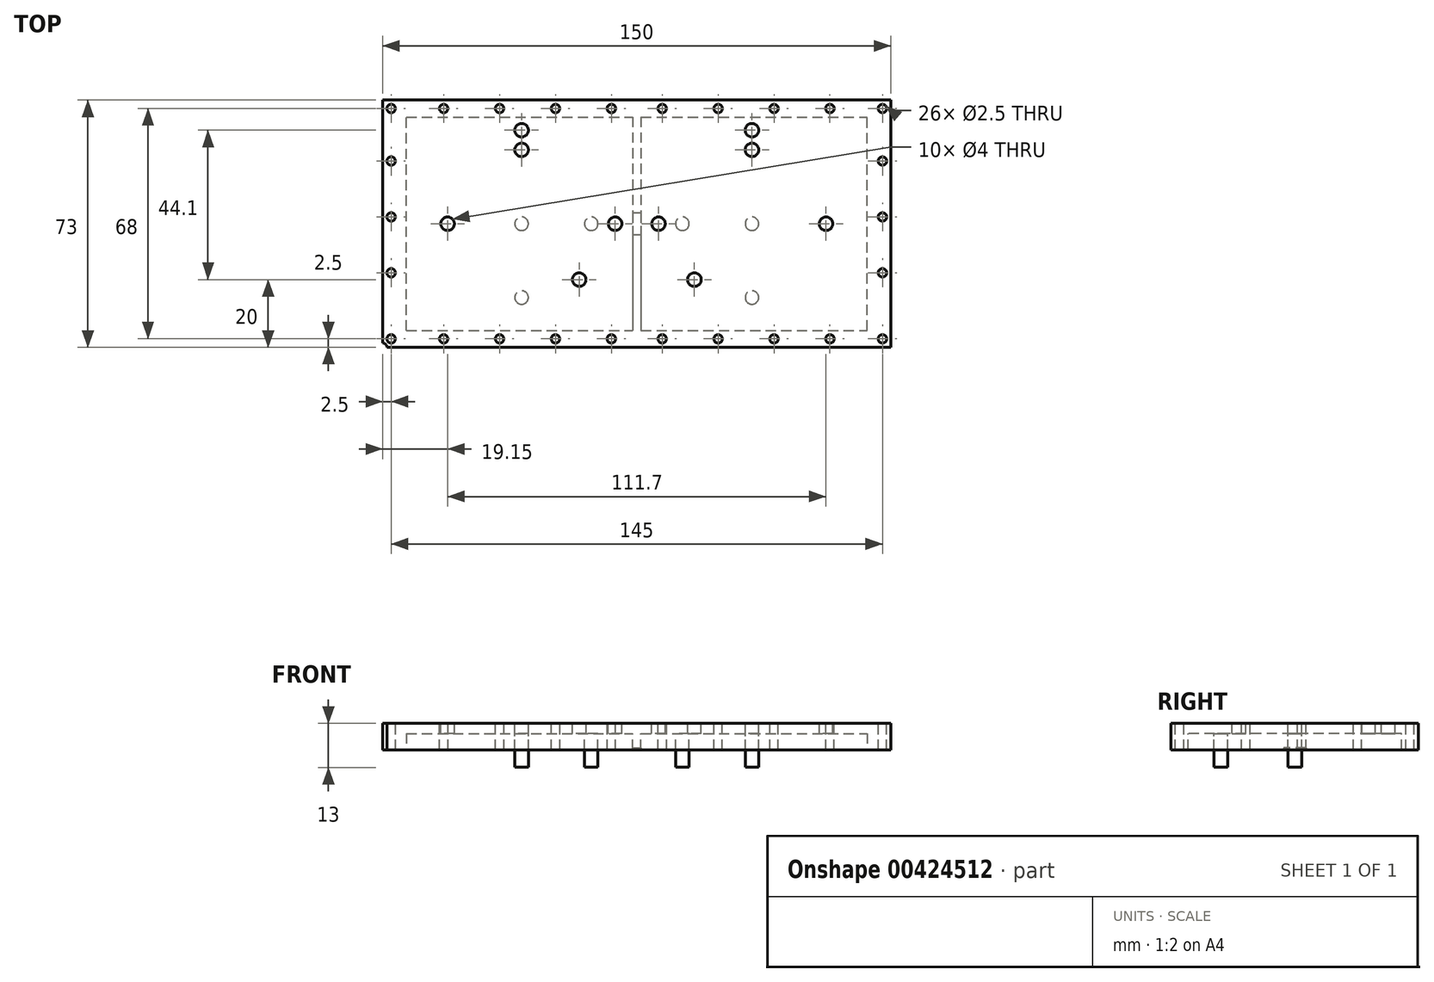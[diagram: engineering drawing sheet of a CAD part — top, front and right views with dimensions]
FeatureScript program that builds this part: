
annotation { "Feature Type Name" : "Feature", "Feature Type Description" : "" }
export const myFeature = defineFeature(function(context is Context, id is Id, definition is map)
    precondition{}
    {
        {
            var Q0;
            Q0=qCreatedBy(makeId("Top.planeOp"),FACE);
            var sketch = newSketch(context, id + "F0", { "sketchPlane" : qUnion([Q0])});
            skLineSegment(sketch, "E0.bottom", {"start": v(0, 0) * mm, "end": v(150, 0) * mm});
            skLineSegment(sketch, "E0.top", {"start": v(0, 73) * mm, "end": v(150, 73) * mm});
            skLineSegment(sketch, "E0.left", {"start": v(0, 0) * mm, "end": v(0, 73) * mm});
            skLineSegment(sketch, "E0.right", {"start": v(150, 0) * mm, "end": v(150, 73) * mm});
            skSolve(sketch);
        }
        {
            var Q0;
            Q0=qSketchRegion(id+"F0",true);
            extrude(context, id + "F1", {"entities" : qUnion([Q0]), "depth" : 7.87 * mm});
        }
        {
            var Q0;
            Q0=qCreatedBy(makeId("Top.planeOp"),FACE);
            var sketch = newSketch(context, id + "F2", { "sketchPlane" : qUnion([Q0])});
            skLineSegment(sketch, "E1.bottom", {"start": v(7, 5) * mm, "end": v(143, 5) * mm});
            skLineSegment(sketch, "E1.top", {"start": v(7, 68) * mm, "end": v(143, 68) * mm});
            skLineSegment(sketch, "E1.left", {"start": v(7, 5) * mm, "end": v(7, 68) * mm});
            skLineSegment(sketch, "E1.right", {"start": v(143, 5) * mm, "end": v(143, 68) * mm});
            skSolve(sketch);
        }
        {
            var Q0;
            Q0=qSketchRegion(id+"F2",true);
            extrude(context, id + "F3", {"entities" : qUnion([Q0]), "operationType" : NewBodyOperationType.REMOVE, "depth" : 4.87 * mm});
        }
        {
            var Q0;
            Q0=makeQuery(id+"F1.opExtrude","CAP_FACE",FACE,{"disambiguationData":[OSD([sQuery(id+"F0.wireOp",EDGE,"E0.bottom"),sQuery(id+"F0.wireOp",EDGE,"E0.top"),sQuery(id+"F0.wireOp",EDGE,"E0.left"),sQuery(id+"F0.wireOp",EDGE,"E0.right")])],"isStart":false});
            var sketch = newSketch(context, id + "F4", { "sketchPlane" : qUnion([Q0])});
            skCircle(sketch, "E2", {"center": v(2.5, 2.5) * mm, "radius": 1.25 * mm});
            skSolve(sketch);
        }
        {
            var Q0;
            Q0=qSketchRegion(id+"F4",true);
            extrude(context, id + "F5", {"entities" : qUnion([Q0]), "operationType" : NewBodyOperationType.REMOVE, "oppositeDirection" : true, "depth" : 7.87 * mm});
        }
        {
            var Q0;
            Q0=makeQuery(id+"F1.opExtrude","CAP_FACE",FACE,{"disambiguationData":[OSD([sQuery(id+"F0.wireOp",EDGE,"E0.bottom"),sQuery(id+"F0.wireOp",EDGE,"E0.top"),sQuery(id+"F0.wireOp",EDGE,"E0.left"),sQuery(id+"F0.wireOp",EDGE,"E0.right")])],"isStart":false});
            var sketch = newSketch(context, id + "F6", { "sketchPlane" : qUnion([Q0])});
            skCircle(sketch, "E3", {"center": v(18, 2.5) * mm, "radius": 1.25 * mm});
            skSolve(sketch);
        }
        {
            var Q0;
            Q0=qSketchRegion(id+"F6",true);
            extrude(context, id + "F7", {"entities" : qUnion([Q0]), "operationType" : NewBodyOperationType.REMOVE, "oppositeDirection" : true, "depth" : 7.87 * mm});
        }
        {
            var Q0;
            Q0=makeQuery(id+"F1.opExtrude","CAP_FACE",FACE,{"disambiguationData":[OSD([sQuery(id+"F0.wireOp",EDGE,"E0.bottom"),sQuery(id+"F0.wireOp",EDGE,"E0.top"),sQuery(id+"F0.wireOp",EDGE,"E0.left"),sQuery(id+"F0.wireOp",EDGE,"E0.right")])],"isStart":false});
            var sketch = newSketch(context, id + "F8", { "sketchPlane" : qUnion([Q0])});
            skCircle(sketch, "E4", {"center": v(34.5, 2.5) * mm, "radius": 1.25 * mm});
            skSolve(sketch);
        }
        {
            var Q0;
            Q0=qSketchRegion(id+"F8",true);
            extrude(context, id + "F9", {"entities" : qUnion([Q0]), "operationType" : NewBodyOperationType.REMOVE, "oppositeDirection" : true, "depth" : 7.87 * mm});
        }
        {
            var Q0;
            Q0=makeQuery(id+"F1.opExtrude","CAP_FACE",FACE,{"disambiguationData":[OSD([sQuery(id+"F0.wireOp",EDGE,"E0.bottom"),sQuery(id+"F0.wireOp",EDGE,"E0.top"),sQuery(id+"F0.wireOp",EDGE,"E0.left"),sQuery(id+"F0.wireOp",EDGE,"E0.right")])],"isStart":false});
            var sketch = newSketch(context, id + "F10", { "sketchPlane" : qUnion([Q0])});
            skCircle(sketch, "E5", {"center": v(51, 2.5) * mm, "radius": 1.25 * mm});
            skSolve(sketch);
        }
        {
            var Q0;
            Q0=qSketchRegion(id+"F10",true);
            extrude(context, id + "F11", {"entities" : qUnion([Q0]), "operationType" : NewBodyOperationType.REMOVE, "oppositeDirection" : true, "depth" : 7.87 * mm});
        }
        {
            var Q0;
            Q0=makeQuery(id+"F1.opExtrude","CAP_FACE",FACE,{"disambiguationData":[OSD([sQuery(id+"F0.wireOp",EDGE,"E0.bottom"),sQuery(id+"F0.wireOp",EDGE,"E0.top"),sQuery(id+"F0.wireOp",EDGE,"E0.left"),sQuery(id+"F0.wireOp",EDGE,"E0.right")])],"isStart":false});
            var sketch = newSketch(context, id + "F12", { "sketchPlane" : qUnion([Q0])});
            skCircle(sketch, "E6", {"center": v(67.5, 2.5) * mm, "radius": 1.25 * mm});
            skSolve(sketch);
        }
        {
            var Q0;
            Q0=qSketchRegion(id+"F12",true);
            extrude(context, id + "F13", {"entities" : qUnion([Q0]), "operationType" : NewBodyOperationType.REMOVE, "oppositeDirection" : true, "depth" : 7.87 * mm});
        }
        {
            var Q0;
            Q0=makeQuery(id+"F1.opExtrude","CAP_FACE",FACE,{"disambiguationData":[OSD([sQuery(id+"F0.wireOp",EDGE,"E0.bottom"),sQuery(id+"F0.wireOp",EDGE,"E0.top"),sQuery(id+"F0.wireOp",EDGE,"E0.left"),sQuery(id+"F0.wireOp",EDGE,"E0.right")])],"isStart":false});
            var sketch = newSketch(context, id + "F14", { "sketchPlane" : qUnion([Q0])});
            skCircle(sketch, "E7", {"center": v(82.5, 2.5) * mm, "radius": 1.25 * mm});
            skSolve(sketch);
        }
        {
            var Q0;
            Q0=qSketchRegion(id+"F14",true);
            extrude(context, id + "F15", {"entities" : qUnion([Q0]), "operationType" : NewBodyOperationType.REMOVE, "oppositeDirection" : true, "depth" : 7.87 * mm});
        }
        {
            var Q0;
            Q0=makeQuery(id+"F1.opExtrude","CAP_FACE",FACE,{"disambiguationData":[OSD([sQuery(id+"F0.wireOp",EDGE,"E0.bottom"),sQuery(id+"F0.wireOp",EDGE,"E0.top"),sQuery(id+"F0.wireOp",EDGE,"E0.left"),sQuery(id+"F0.wireOp",EDGE,"E0.right")])],"isStart":false});
            var sketch = newSketch(context, id + "F16", { "sketchPlane" : qUnion([Q0])});
            skCircle(sketch, "E8", {"center": v(99, 2.5) * mm, "radius": 1.25 * mm});
            skSolve(sketch);
        }
        {
            var Q0;
            Q0=qSketchRegion(id+"F16",true);
            extrude(context, id + "F17", {"entities" : qUnion([Q0]), "operationType" : NewBodyOperationType.REMOVE, "oppositeDirection" : true, "depth" : 7.87 * mm});
        }
        {
            var Q0;
            Q0=makeQuery(id+"F1.opExtrude","CAP_FACE",FACE,{"disambiguationData":[OSD([sQuery(id+"F0.wireOp",EDGE,"E0.bottom"),sQuery(id+"F0.wireOp",EDGE,"E0.top"),sQuery(id+"F0.wireOp",EDGE,"E0.left"),sQuery(id+"F0.wireOp",EDGE,"E0.right")])],"isStart":false});
            var sketch = newSketch(context, id + "F18", { "sketchPlane" : qUnion([Q0])});
            skCircle(sketch, "E9", {"center": v(115.5, 2.5) * mm, "radius": 1.25 * mm});
            skSolve(sketch);
        }
        {
            var Q0;
            Q0=qSketchRegion(id+"F18",true);
            extrude(context, id + "F19", {"entities" : qUnion([Q0]), "operationType" : NewBodyOperationType.REMOVE, "oppositeDirection" : true, "depth" : 7.87 * mm});
        }
        {
            var Q0;
            Q0=makeQuery(id+"F1.opExtrude","CAP_FACE",FACE,{"disambiguationData":[OSD([sQuery(id+"F0.wireOp",EDGE,"E0.bottom"),sQuery(id+"F0.wireOp",EDGE,"E0.top"),sQuery(id+"F0.wireOp",EDGE,"E0.left"),sQuery(id+"F0.wireOp",EDGE,"E0.right")])],"isStart":false});
            var sketch = newSketch(context, id + "F20", { "sketchPlane" : qUnion([Q0])});
            skCircle(sketch, "E10", {"center": v(132, 2.5) * mm, "radius": 1.25 * mm});
            skSolve(sketch);
        }
        {
            var Q0;
            Q0=qSketchRegion(id+"F20",true);
            extrude(context, id + "F21", {"entities" : qUnion([Q0]), "operationType" : NewBodyOperationType.REMOVE, "oppositeDirection" : true, "depth" : 7.87 * mm});
        }
        {
            var Q0;
            Q0=makeQuery(id+"F1.opExtrude","CAP_FACE",FACE,{"disambiguationData":[OSD([sQuery(id+"F0.wireOp",EDGE,"E0.bottom"),sQuery(id+"F0.wireOp",EDGE,"E0.top"),sQuery(id+"F0.wireOp",EDGE,"E0.left"),sQuery(id+"F0.wireOp",EDGE,"E0.right")])],"isStart":false});
            var sketch = newSketch(context, id + "F22", { "sketchPlane" : qUnion([Q0])});
            skCircle(sketch, "E11", {"center": v(147.5, 2.5) * mm, "radius": 1.25 * mm});
            skSolve(sketch);
        }
        {
            var Q0;
            Q0=qSketchRegion(id+"F22",true);
            extrude(context, id + "F23", {"entities" : qUnion([Q0]), "operationType" : NewBodyOperationType.REMOVE, "oppositeDirection" : true, "depth" : 7.87 * mm});
        }
        {
            var Q0;
            Q0=makeQuery(id+"F1.opExtrude","CAP_FACE",FACE,{"disambiguationData":[OSD([sQuery(id+"F0.wireOp",EDGE,"E0.bottom"),sQuery(id+"F0.wireOp",EDGE,"E0.top"),sQuery(id+"F0.wireOp",EDGE,"E0.left"),sQuery(id+"F0.wireOp",EDGE,"E0.right")])],"isStart":false});
            var sketch = newSketch(context, id + "F24", { "sketchPlane" : qUnion([Q0])});
            skCircle(sketch, "E12", {"center": v(2.5, 22) * mm, "radius": 1.25 * mm});
            skSolve(sketch);
        }
        {
            var Q0;
            Q0=qSketchRegion(id+"F24",true);
            extrude(context, id + "F25", {"entities" : qUnion([Q0]), "operationType" : NewBodyOperationType.REMOVE, "oppositeDirection" : true, "depth" : 7.87 * mm});
        }
        {
            var Q0;
            Q0=makeQuery(id+"F1.opExtrude","CAP_FACE",FACE,{"disambiguationData":[OSD([sQuery(id+"F0.wireOp",EDGE,"E0.bottom"),sQuery(id+"F0.wireOp",EDGE,"E0.top"),sQuery(id+"F0.wireOp",EDGE,"E0.left"),sQuery(id+"F0.wireOp",EDGE,"E0.right")])],"isStart":false});
            var sketch = newSketch(context, id + "F26", { "sketchPlane" : qUnion([Q0])});
            skCircle(sketch, "E13", {"center": v(147.5, 22) * mm, "radius": 1.25 * mm});
            skSolve(sketch);
        }
        {
            var Q0;
            Q0=qSketchRegion(id+"F26",true);
            extrude(context, id + "F27", {"entities" : qUnion([Q0]), "operationType" : NewBodyOperationType.REMOVE, "oppositeDirection" : true, "depth" : 7.87 * mm});
        }
        {
            var Q0;
            Q0=makeQuery(id+"F1.opExtrude","CAP_FACE",FACE,{"disambiguationData":[OSD([sQuery(id+"F0.wireOp",EDGE,"E0.bottom"),sQuery(id+"F0.wireOp",EDGE,"E0.top"),sQuery(id+"F0.wireOp",EDGE,"E0.left"),sQuery(id+"F0.wireOp",EDGE,"E0.right")])],"isStart":false});
            var sketch = newSketch(context, id + "F28", { "sketchPlane" : qUnion([Q0])});
            skCircle(sketch, "E14", {"center": v(147.5, 38.5) * mm, "radius": 1.25 * mm});
            skSolve(sketch);
        }
        {
            var Q0;
            Q0=qSketchRegion(id+"F28",true);
            extrude(context, id + "F29", {"entities" : qUnion([Q0]), "operationType" : NewBodyOperationType.REMOVE, "oppositeDirection" : true, "depth" : 7.87 * mm});
        }
        {
            var Q0;
            Q0=makeQuery(id+"F1.opExtrude","CAP_FACE",FACE,{"disambiguationData":[OSD([sQuery(id+"F0.wireOp",EDGE,"E0.bottom"),sQuery(id+"F0.wireOp",EDGE,"E0.top"),sQuery(id+"F0.wireOp",EDGE,"E0.left"),sQuery(id+"F0.wireOp",EDGE,"E0.right")])],"isStart":false});
            var sketch = newSketch(context, id + "F30", { "sketchPlane" : qUnion([Q0])});
            skCircle(sketch, "E15", {"center": v(2.5, 38.5) * mm, "radius": 1.25 * mm});
            skSolve(sketch);
        }
        {
            var Q0;
            Q0=qSketchRegion(id+"F30",true);
            extrude(context, id + "F31", {"entities" : qUnion([Q0]), "operationType" : NewBodyOperationType.REMOVE, "oppositeDirection" : true, "depth" : 7.87 * mm});
        }
        {
            var Q0;
            Q0=makeQuery(id+"F1.opExtrude","CAP_FACE",FACE,{"disambiguationData":[OSD([sQuery(id+"F0.wireOp",EDGE,"E0.bottom"),sQuery(id+"F0.wireOp",EDGE,"E0.top"),sQuery(id+"F0.wireOp",EDGE,"E0.left"),sQuery(id+"F0.wireOp",EDGE,"E0.right")])],"isStart":false});
            var sketch = newSketch(context, id + "F32", { "sketchPlane" : qUnion([Q0])});
            skCircle(sketch, "E16", {"center": v(2.5, 55) * mm, "radius": 1.25 * mm});
            skSolve(sketch);
        }
        {
            var Q0;
            Q0=qSketchRegion(id+"F32",true);
            extrude(context, id + "F33", {"entities" : qUnion([Q0]), "operationType" : NewBodyOperationType.REMOVE, "oppositeDirection" : true, "depth" : 7.87 * mm});
        }
        {
            var Q0;
            Q0=makeQuery(id+"F1.opExtrude","CAP_FACE",FACE,{"disambiguationData":[OSD([sQuery(id+"F0.wireOp",EDGE,"E0.bottom"),sQuery(id+"F0.wireOp",EDGE,"E0.top"),sQuery(id+"F0.wireOp",EDGE,"E0.left"),sQuery(id+"F0.wireOp",EDGE,"E0.right")])],"isStart":false});
            var sketch = newSketch(context, id + "F34", { "sketchPlane" : qUnion([Q0])});
            skCircle(sketch, "E17", {"center": v(147.5, 55) * mm, "radius": 1.25 * mm});
            skSolve(sketch);
        }
        {
            var Q0;
            Q0=qSketchRegion(id+"F34",true);
            extrude(context, id + "F35", {"entities" : qUnion([Q0]), "operationType" : NewBodyOperationType.REMOVE, "oppositeDirection" : true, "depth" : 7.87 * mm});
        }
        {
            var Q0;
            Q0=makeQuery(id+"F1.opExtrude","CAP_FACE",FACE,{"disambiguationData":[OSD([sQuery(id+"F0.wireOp",EDGE,"E0.bottom"),sQuery(id+"F0.wireOp",EDGE,"E0.top"),sQuery(id+"F0.wireOp",EDGE,"E0.left"),sQuery(id+"F0.wireOp",EDGE,"E0.right")])],"isStart":false});
            var sketch = newSketch(context, id + "F36", { "sketchPlane" : qUnion([Q0])});
            skCircle(sketch, "E18", {"center": v(2.5, 70.5) * mm, "radius": 1.25 * mm});
            skSolve(sketch);
        }
        {
            var Q0;
            Q0=qSketchRegion(id+"F36",true);
            extrude(context, id + "F37", {"entities" : qUnion([Q0]), "operationType" : NewBodyOperationType.REMOVE, "oppositeDirection" : true, "depth" : 7.87 * mm});
        }
        {
            var Q0;
            Q0=makeQuery(id+"F1.opExtrude","CAP_FACE",FACE,{"disambiguationData":[OSD([sQuery(id+"F0.wireOp",EDGE,"E0.bottom"),sQuery(id+"F0.wireOp",EDGE,"E0.top"),sQuery(id+"F0.wireOp",EDGE,"E0.left"),sQuery(id+"F0.wireOp",EDGE,"E0.right")])],"isStart":false});
            var sketch = newSketch(context, id + "F38", { "sketchPlane" : qUnion([Q0])});
            skCircle(sketch, "E19", {"center": v(147.5, 70.5) * mm, "radius": 1.25 * mm});
            skSolve(sketch);
        }
        {
            var Q0;
            Q0=qSketchRegion(id+"F38",true);
            extrude(context, id + "F39", {"entities" : qUnion([Q0]), "operationType" : NewBodyOperationType.REMOVE, "oppositeDirection" : true, "depth" : 7.87 * mm});
        }
        {
            var Q0;
            Q0=makeQuery(id+"F1.opExtrude","CAP_FACE",FACE,{"disambiguationData":[OSD([sQuery(id+"F0.wireOp",EDGE,"E0.bottom"),sQuery(id+"F0.wireOp",EDGE,"E0.top"),sQuery(id+"F0.wireOp",EDGE,"E0.left"),sQuery(id+"F0.wireOp",EDGE,"E0.right")])],"isStart":false});
            var sketch = newSketch(context, id + "F40", { "sketchPlane" : qUnion([Q0])});
            skCircle(sketch, "E20", {"center": v(18, 70.5) * mm, "radius": 1.25 * mm});
            skSolve(sketch);
        }
        {
            var Q0;
            Q0=qSketchRegion(id+"F40",true);
            extrude(context, id + "F41", {"entities" : qUnion([Q0]), "operationType" : NewBodyOperationType.REMOVE, "oppositeDirection" : true, "depth" : 7.87 * mm});
        }
        {
            var Q0;
            Q0=makeQuery(id+"F1.opExtrude","CAP_FACE",FACE,{"disambiguationData":[OSD([sQuery(id+"F0.wireOp",EDGE,"E0.bottom"),sQuery(id+"F0.wireOp",EDGE,"E0.top"),sQuery(id+"F0.wireOp",EDGE,"E0.left"),sQuery(id+"F0.wireOp",EDGE,"E0.right")])],"isStart":false});
            var sketch = newSketch(context, id + "F42", { "sketchPlane" : qUnion([Q0])});
            skCircle(sketch, "E21", {"center": v(132, 70.5) * mm, "radius": 1.25 * mm});
            skSolve(sketch);
        }
        {
            var Q0;
            Q0=qSketchRegion(id+"F42",true);
            extrude(context, id + "F43", {"entities" : qUnion([Q0]), "operationType" : NewBodyOperationType.REMOVE, "oppositeDirection" : true, "depth" : 7.87 * mm});
        }
        {
            var Q0;
            Q0=makeQuery(id+"F1.opExtrude","CAP_FACE",FACE,{"disambiguationData":[OSD([sQuery(id+"F0.wireOp",EDGE,"E0.bottom"),sQuery(id+"F0.wireOp",EDGE,"E0.top"),sQuery(id+"F0.wireOp",EDGE,"E0.left"),sQuery(id+"F0.wireOp",EDGE,"E0.right")])],"isStart":false});
            var sketch = newSketch(context, id + "F44", { "sketchPlane" : qUnion([Q0])});
            skCircle(sketch, "E22", {"center": v(34.5, 70.5) * mm, "radius": 1.25 * mm});
            skCircle(sketch, "E23", {"center": v(0, 0) * mm, "radius": 1.25 * mm});
            skSolve(sketch);
        }
        {
            var Q0;
            Q0=qSketchRegion(id+"F44",true);
            extrude(context, id + "F45", {"entities" : qUnion([Q0]), "operationType" : NewBodyOperationType.REMOVE, "oppositeDirection" : true, "depth" : 7.87 * mm});
        }
        {
            var Q0;
            Q0=makeQuery(id+"F1.opExtrude","CAP_FACE",FACE,{"disambiguationData":[OSD([sQuery(id+"F0.wireOp",EDGE,"E0.bottom"),sQuery(id+"F0.wireOp",EDGE,"E0.top"),sQuery(id+"F0.wireOp",EDGE,"E0.left"),sQuery(id+"F0.wireOp",EDGE,"E0.right")])],"isStart":false});
            var sketch = newSketch(context, id + "F46", { "sketchPlane" : qUnion([Q0])});
            skCircle(sketch, "E24", {"center": v(115.5, 70.5) * mm, "radius": 1.25 * mm});
            skSolve(sketch);
        }
        {
            var Q0;
            Q0=qSketchRegion(id+"F46",true);
            extrude(context, id + "F47", {"entities" : qUnion([Q0]), "operationType" : NewBodyOperationType.REMOVE, "oppositeDirection" : true, "depth" : 7.87 * mm});
        }
        {
            var Q0;
            Q0=makeQuery(id+"F1.opExtrude","CAP_FACE",FACE,{"disambiguationData":[OSD([sQuery(id+"F0.wireOp",EDGE,"E0.bottom"),sQuery(id+"F0.wireOp",EDGE,"E0.top"),sQuery(id+"F0.wireOp",EDGE,"E0.left"),sQuery(id+"F0.wireOp",EDGE,"E0.right")])],"isStart":false});
            var sketch = newSketch(context, id + "F48", { "sketchPlane" : qUnion([Q0])});
            skCircle(sketch, "E25", {"center": v(51, 70.5) * mm, "radius": 1.25 * mm});
            skSolve(sketch);
        }
        {
            var Q0;
            Q0=qSketchRegion(id+"F48",true);
            extrude(context, id + "F49", {"entities" : qUnion([Q0]), "operationType" : NewBodyOperationType.REMOVE, "oppositeDirection" : true, "depth" : 7.87 * mm});
        }
        {
            var Q0;
            Q0=makeQuery(id+"F1.opExtrude","CAP_FACE",FACE,{"disambiguationData":[OSD([sQuery(id+"F0.wireOp",EDGE,"E0.bottom"),sQuery(id+"F0.wireOp",EDGE,"E0.top"),sQuery(id+"F0.wireOp",EDGE,"E0.left"),sQuery(id+"F0.wireOp",EDGE,"E0.right")])],"isStart":false});
            var sketch = newSketch(context, id + "F50", { "sketchPlane" : qUnion([Q0])});
            skCircle(sketch, "E26", {"center": v(67.5, 70.5) * mm, "radius": 1.25 * mm});
            skSolve(sketch);
        }
        {
            var Q0;
            Q0=qSketchRegion(id+"F50",true);
            extrude(context, id + "F51", {"entities" : qUnion([Q0]), "operationType" : NewBodyOperationType.REMOVE, "oppositeDirection" : true, "depth" : 7.87 * mm});
        }
        {
            var Q0;
            Q0=makeQuery(id+"F1.opExtrude","CAP_FACE",FACE,{"disambiguationData":[OSD([sQuery(id+"F0.wireOp",EDGE,"E0.bottom"),sQuery(id+"F0.wireOp",EDGE,"E0.top"),sQuery(id+"F0.wireOp",EDGE,"E0.left"),sQuery(id+"F0.wireOp",EDGE,"E0.right")])],"isStart":false});
            var sketch = newSketch(context, id + "F52", { "sketchPlane" : qUnion([Q0])});
            skCircle(sketch, "E27", {"center": v(82.5, 70.5) * mm, "radius": 1.25 * mm});
            skSolve(sketch);
        }
        {
            var Q0;
            Q0=qSketchRegion(id+"F52",true);
            extrude(context, id + "F53", {"entities" : qUnion([Q0]), "operationType" : NewBodyOperationType.REMOVE, "oppositeDirection" : true, "depth" : 7.87 * mm});
        }
        {
            var Q0;
            Q0=makeQuery(id+"F1.opExtrude","CAP_FACE",FACE,{"disambiguationData":[OSD([sQuery(id+"F0.wireOp",EDGE,"E0.bottom"),sQuery(id+"F0.wireOp",EDGE,"E0.top"),sQuery(id+"F0.wireOp",EDGE,"E0.left"),sQuery(id+"F0.wireOp",EDGE,"E0.right")])],"isStart":false});
            var sketch = newSketch(context, id + "F54", { "sketchPlane" : qUnion([Q0])});
            skCircle(sketch, "E28", {"center": v(99, 70.5) * mm, "radius": 1.25 * mm});
            skSolve(sketch);
        }
        {
            var Q0;
            Q0=qSketchRegion(id+"F54",true);
            extrude(context, id + "F55", {"entities" : qUnion([Q0]), "operationType" : NewBodyOperationType.REMOVE, "oppositeDirection" : true, "depth" : 7.87 * mm});
        }
        {
            var Q0;
            Q0=makeQuery(id+"F1.opExtrude","CAP_FACE",FACE,{"disambiguationData":[OSD([sQuery(id+"F0.wireOp",EDGE,"E0.bottom"),sQuery(id+"F0.wireOp",EDGE,"E0.top"),sQuery(id+"F0.wireOp",EDGE,"E0.left"),sQuery(id+"F0.wireOp",EDGE,"E0.right")])],"isStart":false});
            var sketch = newSketch(context, id + "F56", { "sketchPlane" : qUnion([Q0])});
            skCircle(sketch, "E29", {"center": v(41, 64.1) * mm, "radius": 2 * mm});
            skSolve(sketch);
        }
        {
            var Q0;
            Q0=qSketchRegion(id+"F56",true);
            extrude(context, id + "F57", {"entities" : qUnion([Q0]), "operationType" : NewBodyOperationType.REMOVE, "oppositeDirection" : true, "depth" : 3 * mm});
        }
        {
            var Q0;
            Q0=makeQuery(id+"F1.opExtrude","CAP_FACE",FACE,{"disambiguationData":[OSD([sQuery(id+"F0.wireOp",EDGE,"E0.bottom"),sQuery(id+"F0.wireOp",EDGE,"E0.top"),sQuery(id+"F0.wireOp",EDGE,"E0.left"),sQuery(id+"F0.wireOp",EDGE,"E0.right")])],"isStart":false});
            var sketch = newSketch(context, id + "F58", { "sketchPlane" : qUnion([Q0])});
            skCircle(sketch, "E30", {"center": v(41, 58.3) * mm, "radius": 2 * mm});
            skSolve(sketch);
        }
        {
            var Q0;
            Q0=qSketchRegion(id+"F58",true);
            extrude(context, id + "F59", {"entities" : qUnion([Q0]), "operationType" : NewBodyOperationType.REMOVE, "oppositeDirection" : true, "depth" : 3 * mm});
        }
        {
            var Q0;
            Q0=makeQuery(id+"F1.opExtrude","CAP_FACE",FACE,{"disambiguationData":[OSD([sQuery(id+"F0.wireOp",EDGE,"E0.bottom"),sQuery(id+"F0.wireOp",EDGE,"E0.top"),sQuery(id+"F0.wireOp",EDGE,"E0.left"),sQuery(id+"F0.wireOp",EDGE,"E0.right")])],"isStart":false});
            var sketch = newSketch(context, id + "F60", { "sketchPlane" : qUnion([Q0])});
            skCircle(sketch, "E31", {"center": v(19.15, 36.5) * mm, "radius": 2 * mm});
            skSolve(sketch);
        }
        {
            var Q0;
            Q0=qSketchRegion(id+"F60",true);
            extrude(context, id + "F61", {"entities" : qUnion([Q0]), "operationType" : NewBodyOperationType.REMOVE, "oppositeDirection" : true, "depth" : 3 * mm});
        }
        {
            var Q0;
            Q0=makeQuery(id+"F1.opExtrude","CAP_FACE",FACE,{"disambiguationData":[OSD([sQuery(id+"F0.wireOp",EDGE,"E0.bottom"),sQuery(id+"F0.wireOp",EDGE,"E0.top"),sQuery(id+"F0.wireOp",EDGE,"E0.left"),sQuery(id+"F0.wireOp",EDGE,"E0.right")])],"isStart":false});
            var sketch = newSketch(context, id + "F62", { "sketchPlane" : qUnion([Q0])});
            skCircle(sketch, "E32", {"center": v(68.6, 36.5) * mm, "radius": 2 * mm});
            skSolve(sketch);
        }
        {
            var Q0;
            Q0=qSketchRegion(id+"F62",true);
            extrude(context, id + "F63", {"entities" : qUnion([Q0]), "operationType" : NewBodyOperationType.REMOVE, "oppositeDirection" : true, "depth" : 3 * mm});
        }
        {
            var Q0;
            Q0=makeQuery(id+"F1.opExtrude","CAP_FACE",FACE,{"disambiguationData":[OSD([sQuery(id+"F0.wireOp",EDGE,"E0.bottom"),sQuery(id+"F0.wireOp",EDGE,"E0.top"),sQuery(id+"F0.wireOp",EDGE,"E0.left"),sQuery(id+"F0.wireOp",EDGE,"E0.right")])],"isStart":false});
            var sketch = newSketch(context, id + "F64", { "sketchPlane" : qUnion([Q0])});
            skCircle(sketch, "E33", {"center": v(109, 64.1) * mm, "radius": 2 * mm});
            skSolve(sketch);
        }
        {
            var Q0;
            Q0=qSketchRegion(id+"F64",true);
            extrude(context, id + "F65", {"entities" : qUnion([Q0]), "operationType" : NewBodyOperationType.REMOVE, "oppositeDirection" : true, "depth" : 3 * mm});
        }
        {
            var Q0;
            Q0=makeQuery(id+"F1.opExtrude","CAP_FACE",FACE,{"disambiguationData":[OSD([sQuery(id+"F0.wireOp",EDGE,"E0.bottom"),sQuery(id+"F0.wireOp",EDGE,"E0.top"),sQuery(id+"F0.wireOp",EDGE,"E0.left"),sQuery(id+"F0.wireOp",EDGE,"E0.right")])],"isStart":false});
            var sketch = newSketch(context, id + "F66", { "sketchPlane" : qUnion([Q0])});
            skCircle(sketch, "E34", {"center": v(109, 58.3) * mm, "radius": 2 * mm});
            skSolve(sketch);
        }
        {
            var Q0;
            Q0=qSketchRegion(id+"F66",true);
            extrude(context, id + "F67", {"entities" : qUnion([Q0]), "operationType" : NewBodyOperationType.REMOVE, "oppositeDirection" : true, "depth" : 3 * mm});
        }
        {
            var Q0;
            Q0=makeQuery(id+"F1.opExtrude","CAP_FACE",FACE,{"disambiguationData":[OSD([sQuery(id+"F0.wireOp",EDGE,"E0.bottom"),sQuery(id+"F0.wireOp",EDGE,"E0.top"),sQuery(id+"F0.wireOp",EDGE,"E0.left"),sQuery(id+"F0.wireOp",EDGE,"E0.right")])],"isStart":false});
            var sketch = newSketch(context, id + "F68", { "sketchPlane" : qUnion([Q0])});
            skCircle(sketch, "E35", {"center": v(81.4, 36.5) * mm, "radius": 2 * mm});
            skSolve(sketch);
        }
        {
            var Q0;
            Q0=qSketchRegion(id+"F68",true);
            extrude(context, id + "F69", {"entities" : qUnion([Q0]), "operationType" : NewBodyOperationType.REMOVE, "oppositeDirection" : true, "depth" : 3 * mm});
        }
        {
            var Q0;
            Q0=makeQuery(id+"F1.opExtrude","CAP_FACE",FACE,{"disambiguationData":[OSD([sQuery(id+"F0.wireOp",EDGE,"E0.bottom"),sQuery(id+"F0.wireOp",EDGE,"E0.top"),sQuery(id+"F0.wireOp",EDGE,"E0.left"),sQuery(id+"F0.wireOp",EDGE,"E0.right")])],"isStart":false});
            var sketch = newSketch(context, id + "F70", { "sketchPlane" : qUnion([Q0])});
            skCircle(sketch, "E36", {"center": v(130.85, 36.5) * mm, "radius": 2 * mm});
            skSolve(sketch);
        }
        {
            var Q0;
            Q0=qSketchRegion(id+"F70",true);
            extrude(context, id + "F71", {"entities" : qUnion([Q0]), "operationType" : NewBodyOperationType.REMOVE, "oppositeDirection" : true, "depth" : 3 * mm});
        }
        {
            var Q0;
            Q0=makeQuery(id+"F1.opExtrude","CAP_FACE",FACE,{"disambiguationData":[OSD([sQuery(id+"F0.wireOp",EDGE,"E0.bottom"),sQuery(id+"F0.wireOp",EDGE,"E0.top"),sQuery(id+"F0.wireOp",EDGE,"E0.left"),sQuery(id+"F0.wireOp",EDGE,"E0.right")])],"isStart":false});
            var sketch = newSketch(context, id + "F72", { "sketchPlane" : qUnion([Q0])});
            skCircle(sketch, "E37", {"center": v(58, 20) * mm, "radius": 2 * mm});
            skSolve(sketch);
        }
        {
            var Q0;
            Q0=qSketchRegion(id+"F72",true);
            extrude(context, id + "F73", {"entities" : qUnion([Q0]), "operationType" : NewBodyOperationType.REMOVE, "oppositeDirection" : true, "depth" : 3 * mm});
        }
        {
            var Q0;
            Q0=makeQuery(id+"F1.opExtrude","CAP_FACE",FACE,{"disambiguationData":[OSD([sQuery(id+"F0.wireOp",EDGE,"E0.bottom"),sQuery(id+"F0.wireOp",EDGE,"E0.top"),sQuery(id+"F0.wireOp",EDGE,"E0.left"),sQuery(id+"F0.wireOp",EDGE,"E0.right")])],"isStart":false});
            var sketch = newSketch(context, id + "F74", { "sketchPlane" : qUnion([Q0])});
            skCircle(sketch, "E38", {"center": v(92, 20) * mm, "radius": 2 * mm});
            skSolve(sketch);
        }
        {
            var Q0;
            Q0=qSketchRegion(id+"F74",true);
            extrude(context, id + "F75", {"entities" : qUnion([Q0]), "operationType" : NewBodyOperationType.REMOVE, "oppositeDirection" : true, "depth" : 3 * mm});
        }
        {
            var Q0;
            Q0=makeQuery(id+"F3.boolean.opBoolean","COPY",FACE,{"derivedFrom":makeQuery(id+"F3.opExtrude","SWEPT_FACE",FACE,{"disambiguationData":[OSD([sQuery(id+"F2.wireOp",EDGE,"E1.bottom")])]})});
            var sketch = newSketch(context, id + "F76", { "sketchPlane" : qUnion([Q0])});
            skLineSegment(sketch, "E39.bottom", {"start": v(-73.75, 0) * mm, "end": v(-76.25, 0) * mm});
            skLineSegment(sketch, "E39.top", {"start": v(-73.75, 4.87) * mm, "end": v(-76.25, 4.87) * mm});
            skLineSegment(sketch, "E39.left", {"start": v(-73.75, 0) * mm, "end": v(-73.75, 4.87) * mm});
            skLineSegment(sketch, "E39.right", {"start": v(-76.25, 0) * mm, "end": v(-76.25, 4.87) * mm});
            skSolve(sketch);
        }
        {
            var Q0;
            Q0=makeQuery(id+"F76.imprint","IMPRINT",FACE,{"disambiguationData":[TD([[makeQuery(id+"F76.imprint","IMPRINT",EDGE,{"derivedFrom":sQuery(id+"F76.wireOp",EDGE,"E39.bottom")}),-1.0]])]});
            extrude(context, id + "F77", {"entities" : qUnion([Q0]), "operationType" : NewBodyOperationType.ADD, "depth" : 63 * mm});
        }
        {
            var Q0;
            Q0=makeQuery(id+"F77.boolean.opBoolean","MERGE",FACE,{"derivedFrom":[makeQuery(id+"F1.opExtrude","CAP_FACE",FACE,{"disambiguationData":[OSD([sQuery(id+"F0.wireOp",EDGE,"E0.bottom"),sQuery(id+"F0.wireOp",EDGE,"E0.top"),sQuery(id+"F0.wireOp",EDGE,"E0.left"),sQuery(id+"F0.wireOp",EDGE,"E0.right")])],"isStart":true}),makeQuery(id+"F77.opExtrude","SWEPT_FACE",FACE,{"disambiguationData":[OSD([sQuery(id+"F76.wireOp",EDGE,"E39.bottom")])]})]});
            var sketch = newSketch(context, id + "F78", { "sketchPlane" : qUnion([Q0])});
            skLineSegment(sketch, "E40.bottom", {"start": v(73.75, -33.25) * mm, "end": v(76.25, -33.25) * mm});
            skLineSegment(sketch, "E40.top", {"start": v(73.75, -39.75) * mm, "end": v(76.25, -39.75) * mm});
            skLineSegment(sketch, "E40.left", {"start": v(73.75, -33.25) * mm, "end": v(73.75, -39.75) * mm});
            skLineSegment(sketch, "E40.right", {"start": v(76.25, -33.25) * mm, "end": v(76.25, -39.75) * mm});
            skSolve(sketch);
        }
        {
            var Q0;
            Q0=qSketchRegion(id+"F78",true);
            extrude(context, id + "F79", {"entities" : qUnion([Q0]), "operationType" : NewBodyOperationType.REMOVE, "oppositeDirection" : true, "depth" : 0.62 * mm});
        }
        {
            var Q0;
            {var subQ0=sQuery(id+"F2.wireOp",EDGE,"E1.top");var subQ1=sQuery(id+"F2.wireOp",EDGE,"E1.bottom");var subQ2=sQuery(id+"F2.wireOp",EDGE,"E1.left");Q0=makeQuery(id+"F77.boolean.opBoolean","SPLIT",FACE,{"disambiguationData":[TD([makeQuery(id+"F3.boolean.opBoolean","COPY",FACE,{"derivedFrom":makeQuery(id+"F3.opExtrude","SWEPT_FACE",FACE,{"disambiguationData":[OSD([subQ2])]})})])],"derivedFrom":makeQuery(id+"F3.boolean.opBoolean","COPY",FACE,{"derivedFrom":makeQuery(id+"F3.opExtrude","CAP_FACE",FACE,{"disambiguationData":[OSD([subQ1,subQ0,subQ2,sQuery(id+"F2.wireOp",EDGE,"E1.right")])],"isStart":false})})});}
            var sketch = newSketch(context, id + "F80", { "sketchPlane" : qUnion([Q0])});
            skCircle(sketch, "E41", {"center": v(41, -14.7) * mm, "radius": 2 * mm});
            skSolve(sketch);
        }
        {
            var Q0;
            Q0 = qSketchRegion(id + "F80", true);
            extrude(context, id + "F81", {"entities" : qUnion([Q0]), "operationType" : NewBodyOperationType.ADD, "depth" : 10 * mm});
        }
        {
            var Q0;
            {var subQ0=sQuery(id+"F2.wireOp",EDGE,"E1.left");var subQ1=sQuery(id+"F2.wireOp",EDGE,"E1.top");var subQ2=sQuery(id+"F2.wireOp",EDGE,"E1.bottom");Q0=makeQuery(id+"F77.boolean.opBoolean","SPLIT",FACE,{"disambiguationData":[TD([makeQuery(id+"F3.boolean.opBoolean","COPY",FACE,{"derivedFrom":makeQuery(id+"F3.opExtrude","SWEPT_FACE",FACE,{"disambiguationData":[OSD([subQ0])]})})])],"derivedFrom":makeQuery(id+"F3.boolean.opBoolean","COPY",FACE,{"derivedFrom":makeQuery(id+"F3.opExtrude","CAP_FACE",FACE,{"disambiguationData":[OSD([subQ2,subQ1,subQ0,sQuery(id+"F2.wireOp",EDGE,"E1.right")])],"isStart":false})})});}
            var sketch = newSketch(context, id + "F82", { "sketchPlane" : qUnion([Q0])});
            skCircle(sketch, "E42", {"center": v(41, -36.5) * mm, "radius": 2 * mm});
            skSolve(sketch);
        }
        {
            var Q0;
            Q0 = qSketchRegion(id + "F82", true);
            extrude(context, id + "F83", {"entities" : qUnion([Q0]), "operationType" : NewBodyOperationType.ADD, "depth" : 10 * mm});
        }
        {
            var Q0;
            {var subQ0=sQuery(id+"F2.wireOp",EDGE,"E1.right");var subQ1=sQuery(id+"F2.wireOp",EDGE,"E1.top");var subQ2=sQuery(id+"F2.wireOp",EDGE,"E1.bottom");Q0=makeQuery(id+"F77.boolean.opBoolean","SPLIT",FACE,{"disambiguationData":[TD([makeQuery(id+"F3.boolean.opBoolean","COPY",FACE,{"derivedFrom":makeQuery(id+"F3.opExtrude","SWEPT_FACE",FACE,{"disambiguationData":[OSD([subQ0])]})})])],"derivedFrom":makeQuery(id+"F3.boolean.opBoolean","COPY",FACE,{"derivedFrom":makeQuery(id+"F3.opExtrude","CAP_FACE",FACE,{"disambiguationData":[OSD([subQ2,subQ1,sQuery(id+"F2.wireOp",EDGE,"E1.left"),subQ0])],"isStart":false})})});}
            var sketch = newSketch(context, id + "F84", { "sketchPlane" : qUnion([Q0])});
            skCircle(sketch, "E43", {"center": v(109, -36.5) * mm, "radius": 2 * mm});
            skSolve(sketch);
        }
        {
            var Q0;
            Q0 = qSketchRegion(id + "F84", true);
            extrude(context, id + "F85", {"entities" : qUnion([Q0]), "operationType" : NewBodyOperationType.ADD, "depth" : 10 * mm});
        }
        {
            var Q0;
            {var subQ0=sQuery(id+"F2.wireOp",EDGE,"E1.right");var subQ1=sQuery(id+"F2.wireOp",EDGE,"E1.top");var subQ2=sQuery(id+"F2.wireOp",EDGE,"E1.bottom");Q0=makeQuery(id+"F77.boolean.opBoolean","SPLIT",FACE,{"disambiguationData":[TD([makeQuery(id+"F3.boolean.opBoolean","COPY",FACE,{"derivedFrom":makeQuery(id+"F3.opExtrude","SWEPT_FACE",FACE,{"disambiguationData":[OSD([subQ0])]})})])],"derivedFrom":makeQuery(id+"F3.boolean.opBoolean","COPY",FACE,{"derivedFrom":makeQuery(id+"F3.opExtrude","CAP_FACE",FACE,{"disambiguationData":[OSD([subQ2,subQ1,sQuery(id+"F2.wireOp",EDGE,"E1.left"),subQ0])],"isStart":false})})});}
            var sketch = newSketch(context, id + "F86", { "sketchPlane" : qUnion([Q0])});
            skCircle(sketch, "E44", {"center": v(109, -14.7) * mm, "radius": 2 * mm});
            skSolve(sketch);
        }
        {
            var Q0;
            Q0 = qSketchRegion(id + "F86", true);
            extrude(context, id + "F87", {"entities" : qUnion([Q0]), "operationType" : NewBodyOperationType.ADD, "depth" : 10 * mm});
        }
        {
            var Q0;
            {var subQ0=sQuery(id+"F2.wireOp",EDGE,"E1.left");var subQ1=sQuery(id+"F2.wireOp",EDGE,"E1.top");var subQ2=sQuery(id+"F2.wireOp",EDGE,"E1.bottom");Q0=makeQuery(id+"F77.boolean.opBoolean","SPLIT",FACE,{"disambiguationData":[TD([makeQuery(id+"F3.boolean.opBoolean","COPY",FACE,{"derivedFrom":makeQuery(id+"F3.opExtrude","SWEPT_FACE",FACE,{"disambiguationData":[OSD([subQ0])]})})])],"derivedFrom":makeQuery(id+"F3.boolean.opBoolean","COPY",FACE,{"derivedFrom":makeQuery(id+"F3.opExtrude","CAP_FACE",FACE,{"disambiguationData":[OSD([subQ2,subQ1,subQ0,sQuery(id+"F2.wireOp",EDGE,"E1.right")])],"isStart":false})})});}
            var sketch = newSketch(context, id + "F88", { "sketchPlane" : qUnion([Q0])});
            skCircle(sketch, "E45", {"center": v(61.55, -36.5) * mm, "radius": 2 * mm});
            skSolve(sketch);
        }
        {
            var Q0;
            Q0 = qSketchRegion(id + "F88", true);
            extrude(context, id + "F89", {"entities" : qUnion([Q0]), "operationType" : NewBodyOperationType.ADD, "depth" : 10 * mm});
        }
        {
            var Q0;
            {var subQ0=sQuery(id+"F2.wireOp",EDGE,"E1.right");var subQ1=sQuery(id+"F2.wireOp",EDGE,"E1.top");var subQ2=sQuery(id+"F2.wireOp",EDGE,"E1.bottom");Q0=makeQuery(id+"F77.boolean.opBoolean","SPLIT",FACE,{"disambiguationData":[TD([makeQuery(id+"F3.boolean.opBoolean","COPY",FACE,{"derivedFrom":makeQuery(id+"F3.opExtrude","SWEPT_FACE",FACE,{"disambiguationData":[OSD([subQ0])]})})])],"derivedFrom":makeQuery(id+"F3.boolean.opBoolean","COPY",FACE,{"derivedFrom":makeQuery(id+"F3.opExtrude","CAP_FACE",FACE,{"disambiguationData":[OSD([subQ2,subQ1,sQuery(id+"F2.wireOp",EDGE,"E1.left"),subQ0])],"isStart":false})})});}
            var sketch = newSketch(context, id + "F90", { "sketchPlane" : qUnion([Q0])});
            skCircle(sketch, "E46", {"center": v(88.45, -36.5) * mm, "radius": 2 * mm});
            skSolve(sketch);
        }
        {
            var Q0;
            Q0 = qSketchRegion(id + "F90", true);
            extrude(context, id + "F91", {"entities" : qUnion([Q0]), "operationType" : NewBodyOperationType.ADD, "depth" : 10 * mm});
        }
    });
